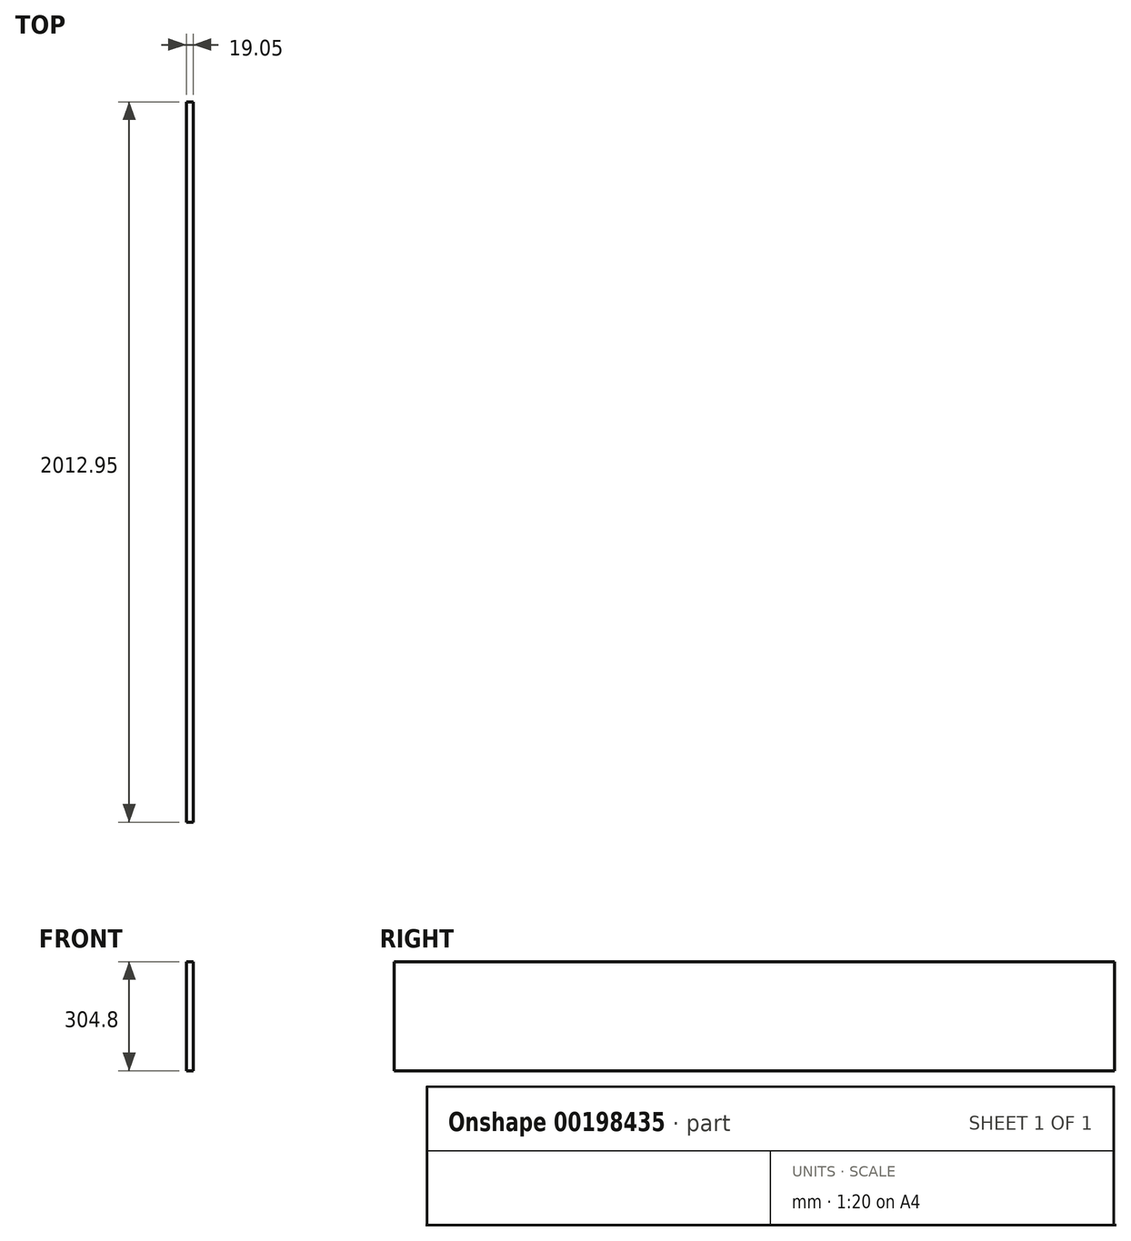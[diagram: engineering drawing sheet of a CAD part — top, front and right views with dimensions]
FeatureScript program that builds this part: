
annotation { "Feature Type Name" : "Feature", "Feature Type Description" : "" }
export const myFeature = defineFeature(function(context is Context, id is Id, definition is map)
    precondition{}
    {
        {
            var Q0;
            Q0=qCreatedBy(makeId("Right.planeOp"),FACE);
            var sketch = newSketch(context, id + "F0", { "sketchPlane" : qUnion([Q0])});
            skLineSegment(sketch, "E0.bottom", {"start": v(0, 0) * mm, "end": v(2012.95, 0) * mm});
            skLineSegment(sketch, "E0.top", {"start": v(0, 304.8) * mm, "end": v(2012.95, 304.8) * mm});
            skLineSegment(sketch, "E0.left", {"start": v(0, 0) * mm, "end": v(0, 304.8) * mm});
            skLineSegment(sketch, "E0.right", {"start": v(2012.95, 0) * mm, "end": v(2012.95, 304.8) * mm});
            skSolve(sketch);
        }
        {
            var Q0;
            Q0 = qSketchRegion(id + "F0", true);
            extrude(context, id + "F1", {"entities" : qUnion([Q0]), "depth" : 19.05 * mm});
        }
    });
